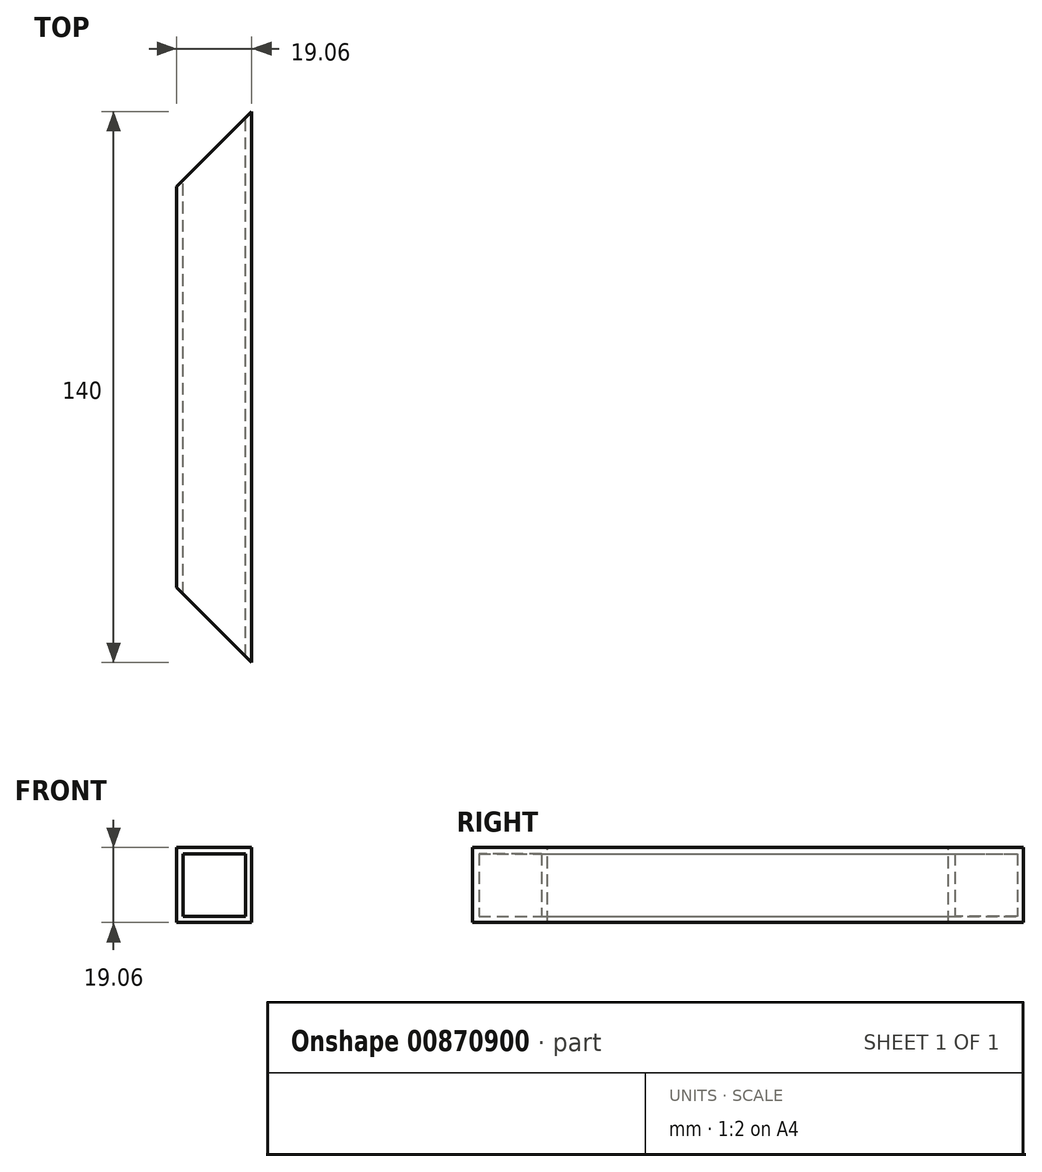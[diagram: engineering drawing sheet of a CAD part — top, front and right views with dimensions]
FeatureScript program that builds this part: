
annotation { "Feature Type Name" : "Feature", "Feature Type Description" : "" }
export const myFeature = defineFeature(function(context is Context, id is Id, definition is map)
    precondition{}
    {
        {
            var Q0;
            Q0=qCreatedBy(makeId("Front.planeOp"),FACE);
            var sketch = newSketch(context, id + "F0", { "sketchPlane" : qUnion([Q0])});
            skLineSegment(sketch, "E0.bottom", {"start": v(9.53, 9.53) * mm, "end": v(-9.53, 9.53) * mm});
            skLineSegment(sketch, "E0.top", {"start": v(9.53, -9.52) * mm, "end": v(-9.53, -9.52) * mm});
            skLineSegment(sketch, "E0.left", {"start": v(9.53, 9.53) * mm, "end": v(9.53, -9.52) * mm});
            skLineSegment(sketch, "E0.right", {"start": v(-9.53, 9.53) * mm, "end": v(-9.53, -9.52) * mm});
            skPoint(sketch, "E0.middle", {"position": v(0, 0) * mm});
            skLineSegment(sketch, "E1.bottom", {"start": v(7.94, 7.94) * mm, "end": v(-7.94, 7.94) * mm});
            skLineSegment(sketch, "E1.top", {"start": v(7.94, -7.94) * mm, "end": v(-7.94, -7.94) * mm});
            skLineSegment(sketch, "E1.left", {"start": v(7.94, 7.94) * mm, "end": v(7.94, -7.94) * mm});
            skLineSegment(sketch, "E1.right", {"start": v(-7.94, 7.94) * mm, "end": v(-7.94, -7.94) * mm});
            skSolve(sketch);
        }
        {
            var Q0;
            Q0=qSketchRegion(id+"F0",true);
            extrude(context, id + "F1", {"entities" : qUnion([Q0]), "depth" : 140 * mm, "offsetDistance" : 25 * mm});
        }
        {
            var Q0;
            Q0=qCreatedBy(makeId("Top.planeOp"),FACE);
            var sketch = newSketch(context, id + "F2", { "sketchPlane" : qUnion([Q0])});
            skLineSegment(sketch, "E2", {"start": v(-9.53, 0) * mm, "end": v(9.53, 0) * mm});
            skLineSegment(sketch, "E3", {"start": v(-9.53, 0) * mm, "end": v(-9.53, -19.05) * mm});
            skLineSegment(sketch, "E4", {"start": v(-9.53, -19.05) * mm, "end": v(9.53, 0) * mm});
            skPoint(sketch, "E5", {"position": v(0, -140) * mm});
            skLineSegment(sketch, "E6", {"start": v(-9.53, -140) * mm, "end": v(9.53, -140) * mm});
            skLineSegment(sketch, "E7", {"start": v(-9.53, -120.95) * mm, "end": v(9.53, -140) * mm});
            skLineSegment(sketch, "E8", {"start": v(-9.53, -140) * mm, "end": v(-9.53, -120.95) * mm});
            skSolve(sketch);
        }
        {
            var Q0;
            Q0 = qSketchRegion(id + "F2", true);
            extrude(context, id + "F3", {"entities" : qUnion([Q0]), "operationType" : NewBodyOperationType.REMOVE, "endBound" : BoundingType.THROUGH_ALL, "oppositeDirection" : true, "depth" : 25 * mm, "offsetDistance" : 25 * mm});
        }
        {
            var Q0;
            Q0 = qSketchRegion(id + "F2", true);
            extrude(context, id + "F4", {"entities" : qUnion([Q0]), "operationType" : NewBodyOperationType.REMOVE, "endBound" : BoundingType.THROUGH_ALL, "depth" : 25 * mm, "offsetDistance" : 25 * mm});
        }
    });
